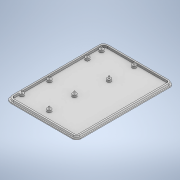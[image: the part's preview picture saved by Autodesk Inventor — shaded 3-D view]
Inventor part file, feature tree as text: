
AUTODESK INVENTOR PART (.ipt)
format: ipt  version: 2022 (Build 260153000, 153)  size: 246,784 bytes
history: native  units: mm
features: extrude x6, sketch x6
ambient origin geometry x8: Origin, YZ Plane, XZ Plane, XY Plane, X Axis, Y Axis, Z Axis, Center Point
bodies: Solid1 (feature_tree)
feature tree (12):
  extrude  "Extrusion1"  Depth=6.0mm TaperAngle=0.0deg
  extrude  "Extrusion2"  Depth=71.58mm
  extrude  "Extrusion3"  Depth=8.0mm
  extrude  "Extrusion4"  Depth=8.0mm
  extrude  "Extrusion5"  Depth=8.0mm
  extrude  "Extrusion6"  Depth=4.0mm
  sketch  "Sketch1"  dims[d3=3.0mm d4=6.0mm d5=0.0mm]
  sketch  "Sketch4"  dims[d9=2.0mm d10=0.0mm d12=71.58mm]
  sketch  "Sketch5"  dims[d13=67.15mm d14=8.0mm]
  sketch  "Sketch6"  dims[d15=8.0mm d16=8.0mm]
  sketch  "Sketch7"  dims[d17=8.0mm d18=8.44mm]
  sketch  "Sketch8"  dims[d19=7.81mm d20=9.533mm d21=8.684mm d22=11.895mm d23=7.81mm d24=7.81mm d25=8.602mm d26=0.0mm d28=10.0mm d29=4.0mm d30=0.0mm d31=2.5mm d32=2.5mm d33=2.5mm d34=2.5mm d35=4.0mm d36=0.0mm d37=75.0mm d38=53.0mm d39=8.0mm d40=8.0mm d41=8.0mm d42=8.0mm d43=14.7mm d44=2.1mm d45=2.1mm d46=13.7mm d47=2.0mm d48=2.0mm d49=7.6mm d50=17.3mm d53=8.0mm d55=50.0mm d56=4.0mm d57=0.0mm d58=2.5mm d59=2.5mm d60=2.5mm d61=2.5mm d62=4.0mm d63=0.0mm]
